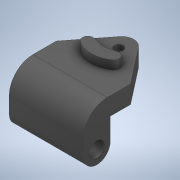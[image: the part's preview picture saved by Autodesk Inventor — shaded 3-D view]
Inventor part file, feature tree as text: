
AUTODESK INVENTOR PART (.ipt)
format: ipt  version: 2020 (Build 240168000, 168)  size: 229,888 bytes
history: native  units: in
note: dims shown in document units (in); Inventor stores cm internally (conversion verified against a paired STEP export)
features: extrude x3, sketch x3, projected_geometry x1
ambient origin geometry x8: Origin, YZ Plane, XZ Plane, XY Plane, X Axis, Y Axis, Z Axis, Center Point
bodies: Solid2 (feature_tree), Solid1 (feature_tree)
feature tree (7):
  extrude  "make bean smaller"  Depth=0.3937in TaperAngle=0.0deg
  extrude  "make bottom plate space bigger"  Depth=0.126in TaperAngle=0.0deg
  extrude  "make standoff hole bigger"  Depth=0.126in TaperAngle=0.0deg
  sketch  "Sketch2"  dims[d7=0.0039in d8=0.3937in d9=0.0in]
  projected_geometry  "Projected Loop1"
  sketch  "Sketch4"  dims[d13=0.0118in d14=0.126in d15=0.0in]
  sketch  "Sketch5"  dims[d16=0.2008in d17=0.126in d18=0.0in]
